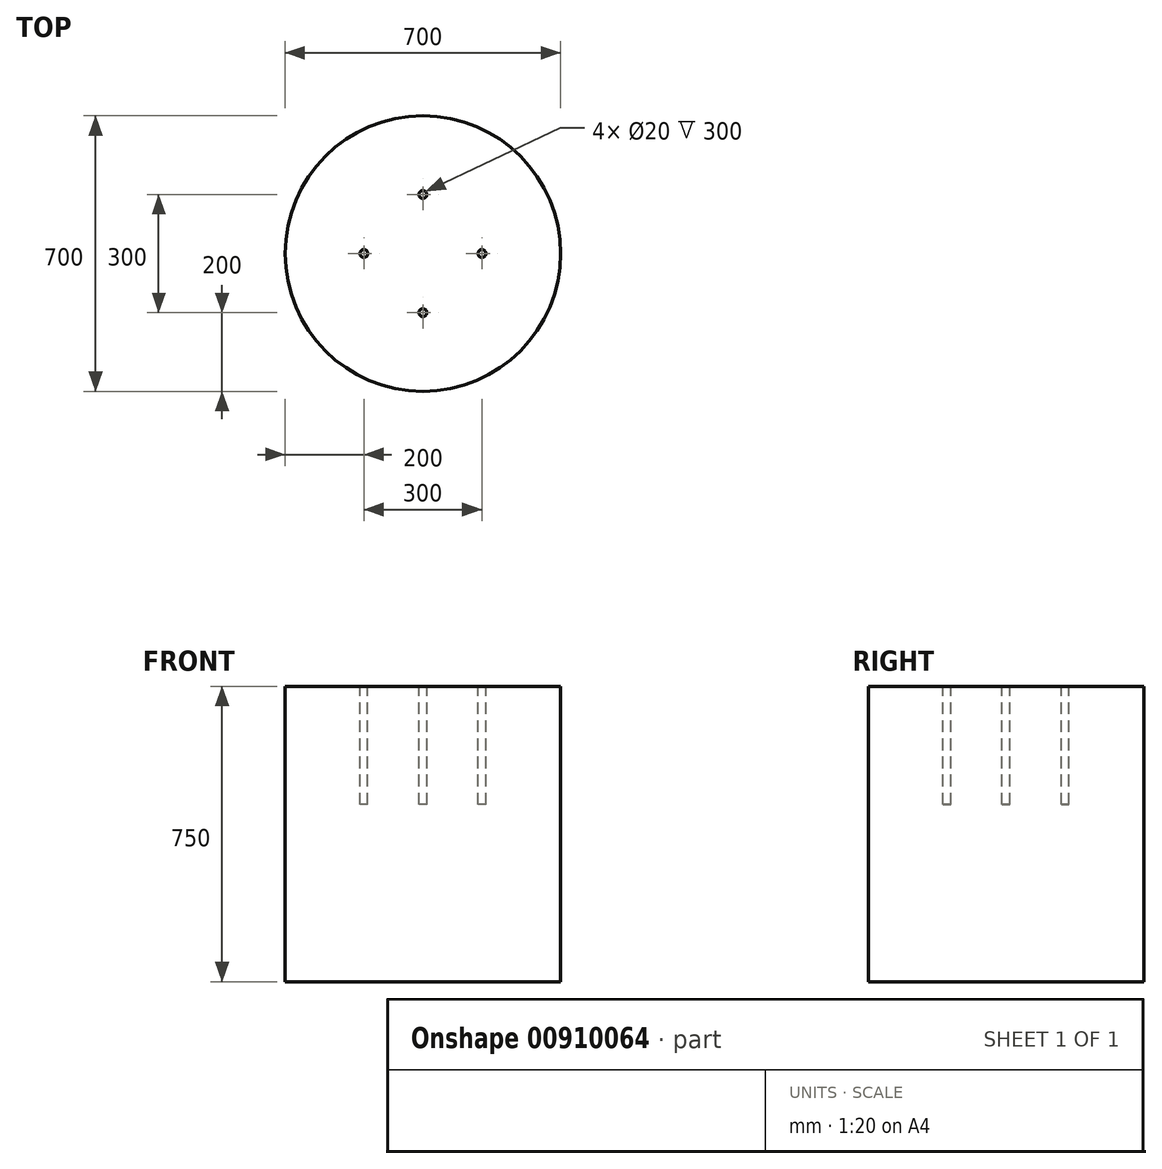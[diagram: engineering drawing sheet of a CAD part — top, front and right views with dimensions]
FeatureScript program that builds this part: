
annotation { "Feature Type Name" : "Feature", "Feature Type Description" : "" }
export const myFeature = defineFeature(function(context is Context, id is Id, definition is map)
    precondition{}
    {
        {
            var Q0;
            Q0=qCreatedBy(makeId("Top.planeOp"),FACE);
            var sketch = newSketch(context, id + "F0", { "sketchPlane" : qUnion([Q0])});
            skCircle(sketch, "E0", {"center": v(0, 0) * mm, "radius": 350 * mm});
            skSolve(sketch);
        }
        {
            var Q0;
            Q0 = qSketchRegion(id + "F0", true);
            extrude(context, id + "F1", {"entities" : qUnion([Q0]), "depth" : 750 * mm, "offsetDistance" : 25 * mm});
        }
        {
            var Q0;
            Q0=makeQuery(id+"F1.opExtrude","CAP_FACE",FACE,{"disambiguationData":[OSD([sQuery(id+"F0.wireOp",EDGE,"E0")])],"isStart":false});
            var sketch = newSketch(context, id + "F2", { "sketchPlane" : qUnion([Q0])});
            skCircle(sketch, "E1", {"center": v(0, 150) * mm, "radius": 10 * mm});
            skCircle(sketch, "E2", {"center": v(0, -150) * mm, "radius": 10 * mm});
            skCircle(sketch, "E3", {"center": v(150, 0) * mm, "radius": 10 * mm});
            skCircle(sketch, "E4", {"center": v(-150, 0) * mm, "radius": 10 * mm});
            skSolve(sketch);
        }
        {
            var Q0;
            Q0=makeQuery(id+"F2.imprint","IMPRINT",FACE,{"disambiguationData":[TD([[makeQuery(id+"F2.imprint","IMPRINT",EDGE,{"derivedFrom":sQuery(id+"F2.wireOp",EDGE,"E4")}),1.0]])]});
            var Q1;
            Q1=makeQuery(id+"F2.imprint","IMPRINT",FACE,{"disambiguationData":[TD([[makeQuery(id+"F2.imprint","IMPRINT",EDGE,{"derivedFrom":sQuery(id+"F2.wireOp",EDGE,"E2")}),1.0]])]});
            var Q2;
            Q2=makeQuery(id+"F2.imprint","IMPRINT",FACE,{"disambiguationData":[TD([[makeQuery(id+"F2.imprint","IMPRINT",EDGE,{"derivedFrom":sQuery(id+"F2.wireOp",EDGE,"E3")}),1.0]])]});
            var Q3;
            Q3=makeQuery(id+"F2.imprint","IMPRINT",FACE,{"disambiguationData":[TD([[makeQuery(id+"F2.imprint","IMPRINT",EDGE,{"derivedFrom":sQuery(id+"F2.wireOp",EDGE,"E1")}),1.0]])]});
            extrude(context, id + "F3", {"entities" : qUnion([Q0, Q1, Q2, Q3]), "operationType" : NewBodyOperationType.REMOVE, "oppositeDirection" : true, "depth" : 300 * mm, "offsetDistance" : 25 * mm});
        }
    });
